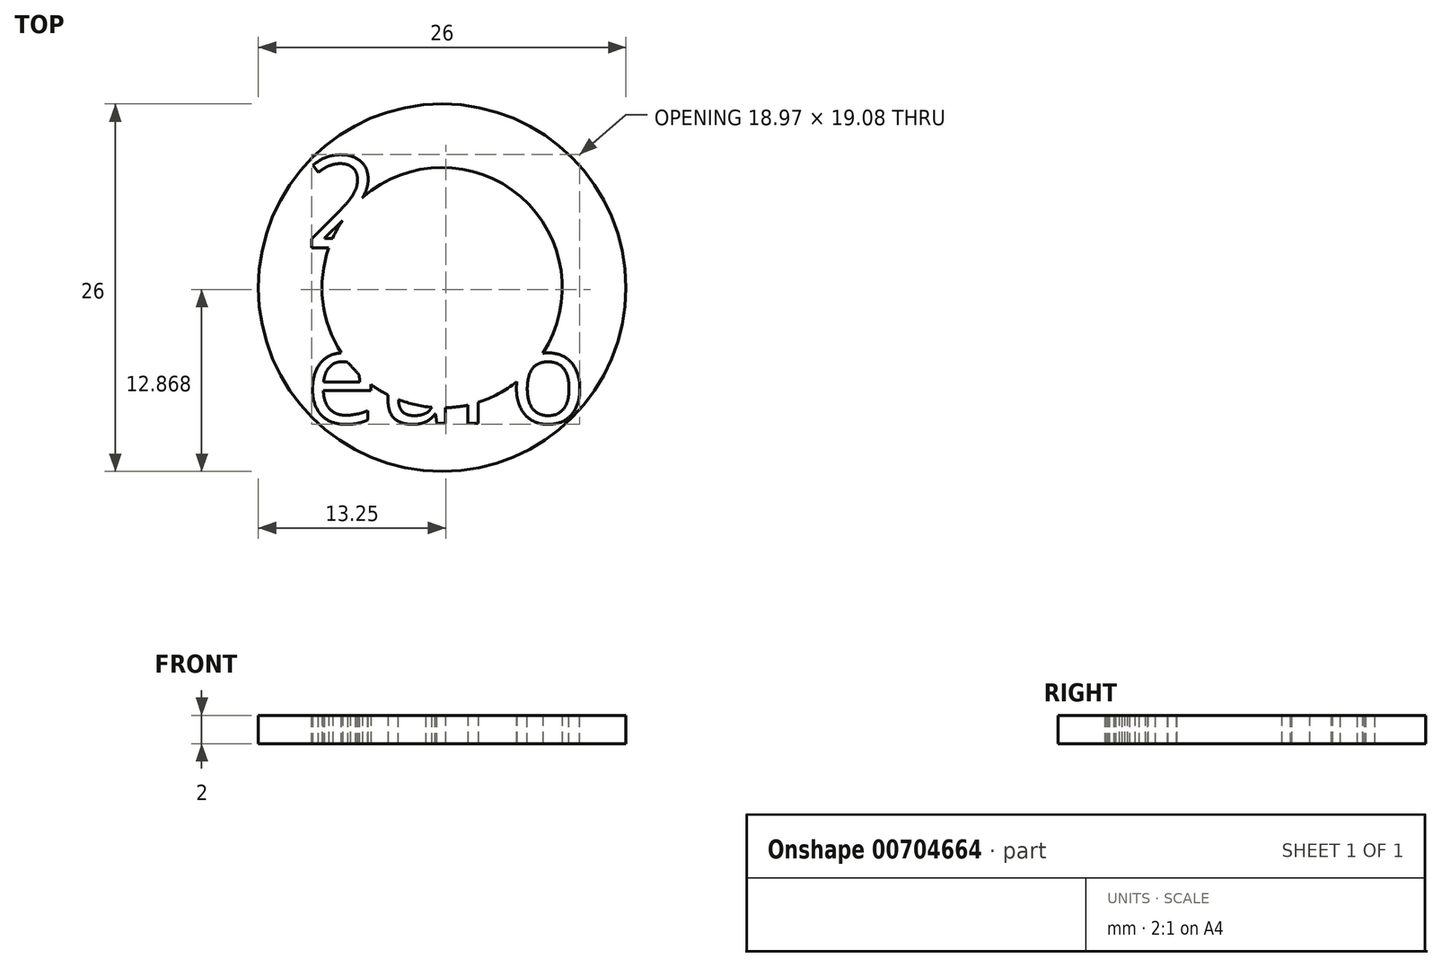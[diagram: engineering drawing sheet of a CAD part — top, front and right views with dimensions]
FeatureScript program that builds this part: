
annotation { "Feature Type Name" : "Feature", "Feature Type Description" : "" }
export const myFeature = defineFeature(function(context is Context, id is Id, definition is map)
    precondition{}
    {
        {
            var Q0;
            Q0=qCreatedBy(makeId("Top.planeOp"),FACE);
            var sketch = newSketch(context, id + "F0", { "sketchPlane" : qUnion([Q0])});
            skArc(sketch, "E0.0", {"start": v(53.58, 21.86) * mm, "mid": v(52.26, 25.04) * mm, "end": v(49.08, 26.36) * mm});
            skLineSegment(sketch, "E0.1", {"start": v(53.58, 15.3) * mm, "end": v(53.58, 21.86) * mm});
            skLineSegment(sketch, "E0.2", {"start": v(49.08, 26.36) * mm, "end": v(-31.42, 26.36) * mm});
            skArc(sketch, "E0.3", {"start": v(53.58, -1.57) * mm, "mid": v(48.8, 6.86) * mm, "end": v(53.58, 15.3) * mm});
            skLineSegment(sketch, "E0.4", {"start": v(53.58, -27.14) * mm, "end": v(53.58, -1.57) * mm});
            skArc(sketch, "E0.5", {"start": v(49.08, -31.64) * mm, "mid": v(52.26, -30.32) * mm, "end": v(53.58, -27.14) * mm});
            skArc(sketch, "E0.6", {"start": v(-31.42, 26.36) * mm, "mid": v(-34.6, 25.04) * mm, "end": v(-35.92, 21.86) * mm});
            skLineSegment(sketch, "E0.7", {"start": v(-35.92, 21.86) * mm, "end": v(-35.92, -27.14) * mm});
            skArc(sketch, "E0.8", {"start": v(-35.92, -27.14) * mm, "mid": v(-34.6, -30.32) * mm, "end": v(-31.42, -31.64) * mm});
            skLineSegment(sketch, "E0.9", {"start": v(-31.42, -31.64) * mm, "end": v(49.08, -31.64) * mm});
            skLineSegment(sketch, "E1", {"start": v(-21.92, -31.64) * mm, "end": v(-21.92, -29.64) * mm});
            skLineSegment(sketch, "E2", {"start": v(-21.92, -29.64) * mm, "end": v(-30.92, -29.64) * mm});
            skLineSegment(sketch, "E3", {"start": v(-30.92, -29.64) * mm, "end": v(-30.92, -31.64) * mm});
            skLineSegment(sketch, "E4", {"start": v(-35.92, 21.86) * mm, "end": v(-33.92, 21.86) * mm});
            skLineSegment(sketch, "E5", {"start": v(-33.92, 21.86) * mm, "end": v(-33.92, 14.36) * mm});
            skLineSegment(sketch, "E6", {"start": v(-33.92, 14.36) * mm, "end": v(-35.92, 14.36) * mm});
            skLineSegment(sketch, "E7", {"start": v(20.08, 26.36) * mm, "end": v(20.08, 24.36) * mm});
            skLineSegment(sketch, "E8", {"start": v(10.08, 24.36) * mm, "end": v(20.08, 24.36) * mm});
            skLineSegment(sketch, "E9", {"start": v(10.08, 24.36) * mm, "end": v(10.08, 26.36) * mm});
            skLineSegment(sketch, "E10", {"start": v(8.83, -31.64) * mm, "end": v(8.83, 26.36) * mm, "construction": true});
            skLineSegment(sketch, "E11", {"start": v(8.83, 26.36) * mm, "end": v(8.83, -2.64) * mm, "construction": true});
            skPoint(sketch, "E12", {"position": v(-6.1, -2.64) * mm});
            skCircle(sketch, "E13", {"center": v(-6.1, -2.64) * mm, "radius": 5 * mm});
            skCircle(sketch, "E14", {"center": v(-6.1, -2.64) * mm, "radius": 2.5 * mm});
            skLineSegment(sketch, "E15", {"start": v(53.58, -1.57) * mm, "end": v(53.58, 15.3) * mm});
            skCircle(sketch, "E16.0", {"center": v(-20.42, -16.14) * mm, "radius": 8.5 * mm});
            skLineSegment(sketch, "E16.1", {"start": v(-20.42, -24.64) * mm, "end": v(38.08, -24.64) * mm});
            skCircle(sketch, "E16.2", {"center": v(38.08, -16.14) * mm, "radius": 8.5 * mm});
            skLineSegment(sketch, "E16.3", {"start": v(38.08, -7.64) * mm, "end": v(-20.42, -7.64) * mm});
            skCircle(sketch, "E17.MirrorC", {"center": v(-20.42, 10.86) * mm, "radius": 8.5 * mm});
            skLineSegment(sketch, "E18.MirrorCS", {"start": v(38.08, 2.36) * mm, "end": v(-20.42, 2.36) * mm});
            skLineSegment(sketch, "E19.MirrorCS", {"start": v(-20.42, 19.36) * mm, "end": v(38.08, 19.36) * mm});
            skCircle(sketch, "E20.MirrorC", {"center": v(38.08, 10.86) * mm, "radius": 8.5 * mm});
            skLineSegment(sketch, "E21", {"start": v(-21.92, -29.64) * mm, "end": v(13.08, -29.64) * mm});
            skLineSegment(sketch, "E22", {"start": v(13.08, -29.64) * mm, "end": v(13.08, -31.64) * mm});
            skLineSegment(sketch, "E23", {"start": v(-33.92, 14.36) * mm, "end": v(-33.92, 2.36) * mm});
            skLineSegment(sketch, "E24", {"start": v(10.08, 24.36) * mm, "end": v(-1.92, 24.36) * mm});
            skLineSegment(sketch, "E25", {"start": v(-1.92, 24.36) * mm, "end": v(-1.92, 26.36) * mm});
            skLineSegment(sketch, "E26", {"start": v(8.83, -2.64) * mm, "end": v(-30.43, -2.64) * mm, "construction": true});
            skLineSegment(sketch, "E27", {"start": v(-33.92, 2.36) * mm, "end": v(-35.92, 2.36) * mm});
            skPoint(sketch, "E28.end.orphan", {"position": v(-35.92, -2.64) * mm});
            skPoint(sketch, "E29.orphan", {"position": v(-33.92, -2.64) * mm});
            skLineSegment(sketch, "E30", {"start": v(22.08, 26.36) * mm, "end": v(22.08, 24.36) * mm});
            skLineSegment(sketch, "E31", {"start": v(22.08, 24.36) * mm, "end": v(20.08, 24.36) * mm});
            skLineSegment(sketch, "E32", {"start": v(-30.92, -29.64) * mm, "end": v(-32.92, -29.64) * mm});
            skLineSegment(sketch, "E33", {"start": v(-32.92, -29.64) * mm, "end": v(-32.92, -31.38) * mm});
            skCircle(sketch, "E34", {"center": v(38.08, 10.86) * mm, "radius": 9.85 * mm});
            skCircle(sketch, "E35", {"center": v(38.08, 10.86) * mm, "radius": 13 * mm});
            skSolve(sketch);
        }
        {
            var Q0;
            {var subQ0=sQuery(id+"F0.wireOp",EDGE,"E35");var subQ1=sQuery(id+"F0.wireOp",EDGE,"E0.3");var subQ2=makeQuery(id+"F0.imprint","INTERSECT",VERTEX,{"disambiguationData":[OD(0.0)],"derivedFrom":[subQ1,subQ0]});Q0=makeQuery(id+"F0.imprint","IMPRINT",FACE,{"disambiguationData":[TD([[makeQuery(id+"F0.imprint","IMPRINT",EDGE,{"disambiguationData":[TD([[subQ2,-1.0]])],"derivedFrom":subQ1}),-1.0]])]});}
            var Q1;
            {var subQ5=sQuery(id+"F0.wireOp",EDGE,"E35");var subQ8=sQuery(id+"F0.wireOp",EDGE,"E0.3");var subQ9=makeQuery(id+"F0.imprint","INTERSECT",VERTEX,{"disambiguationData":[OD(0.0)],"derivedFrom":[subQ8,subQ5]});Q1=makeQuery(id+"F0.imprint","IMPRINT",FACE,{"disambiguationData":[TD([[makeQuery(id+"F0.imprint","IMPRINT",EDGE,{"disambiguationData":[TD([[subQ9,-1.0]])],"derivedFrom":subQ8}),1.0]])]});}
            var Q2;
            {var subQ0=sQuery(id+"F0.wireOp",EDGE,"E34");var subQ1=sQuery(id+"F0.wireOp",EDGE,"E18.MirrorCS");var subQ2=makeQuery(id+"F0.imprint","INTERSECT",VERTEX,{"derivedFrom":[subQ1,subQ0]});Q2=makeQuery(id+"F0.imprint","IMPRINT",FACE,{"disambiguationData":[TD([[makeQuery(id+"F0.imprint","IMPRINT",EDGE,{"disambiguationData":[TD([[subQ2,-1.0]])],"derivedFrom":subQ1}),-1.0]])]});}
            var Q3;
            {var subQ0=sQuery(id+"F0.wireOp",EDGE,"E20.MirrorC");var subQ1=sQuery(id+"F0.wireOp",EDGE,"E18.MirrorCS");var subQ2=makeQuery(id+"F0.imprint","INTERSECT",VERTEX,{"derivedFrom":[subQ1,subQ0]});Q3=makeQuery(id+"F0.imprint","IMPRINT",FACE,{"disambiguationData":[TD([[makeQuery(id+"F0.imprint","IMPRINT",EDGE,{"disambiguationData":[TD([[subQ2,-1.0]])],"derivedFrom":subQ1}),-1.0]])]});}
            var Q4;
            {var subQ0=sQuery(id+"F0.wireOp",EDGE,"E20.MirrorC");var subQ1=makeQuery(id+"F0.imprint","INTERSECT",VERTEX,{"derivedFrom":[sQuery(id+"F0.wireOp",EDGE,"E18.MirrorCS"),subQ0]});Q4=makeQuery(id+"F0.imprint","IMPRINT",FACE,{"disambiguationData":[TD([[makeQuery(id+"F0.imprint","IMPRINT",EDGE,{"disambiguationData":[TD([[subQ1,1.0]])],"derivedFrom":subQ0}),-1.0]])]});}
            var Q5;
            {var subQ0=sQuery(id+"F0.wireOp",EDGE,"E20.MirrorC");var subQ1=sQuery(id+"F0.wireOp",EDGE,"E18.MirrorCS");var subQ2=makeQuery(id+"F0.imprint","INTERSECT",VERTEX,{"derivedFrom":[subQ1,subQ0]});Q5=makeQuery(id+"F0.imprint","IMPRINT",FACE,{"disambiguationData":[TD([[makeQuery(id+"F0.imprint","IMPRINT",EDGE,{"disambiguationData":[TD([[subQ2,-1.0]])],"derivedFrom":subQ1}),1.0]])]});}
            extrude(context, id + "F1", {"entities" : qUnion([Q0, Q1, Q2, Q3, Q4, Q5]), "depth" : 2 * mm, "offsetDistance" : 25 * mm});
        }
        {
            var Q0;
            Q0=makeQuery(id+"F1.opExtrude","CAP_FACE",FACE,{"disambiguationData":[OSD([sQuery(id+"F0.wireOp",EDGE,"E35")])],"isStart":false});
            var sketch = newSketch(context, id + "F2", { "sketchPlane" : qUnion([Q0])});
            skText(sketch, "E36", { "text": "2\neuro", "fontName": "OpenSans-Regular.ttf"});
            const initialGuessF2  = {"E36": [0.0284, 0.01367, 1, 0, 0.00656]};
            skSetInitialGuess(sketch, initialGuessF2);
            skSolve(sketch);
        }
        {
            var Q0;
            Q0 = qSketchRegion(id + "F2", true);
            extrude(context, id + "F3", {"entities" : qUnion([Q0]), "operationType" : NewBodyOperationType.REMOVE, "endBound" : BoundingType.THROUGH_ALL, "oppositeDirection" : true, "depth" : 25 * mm, "offsetDistance" : 25 * mm});
        }
    });
